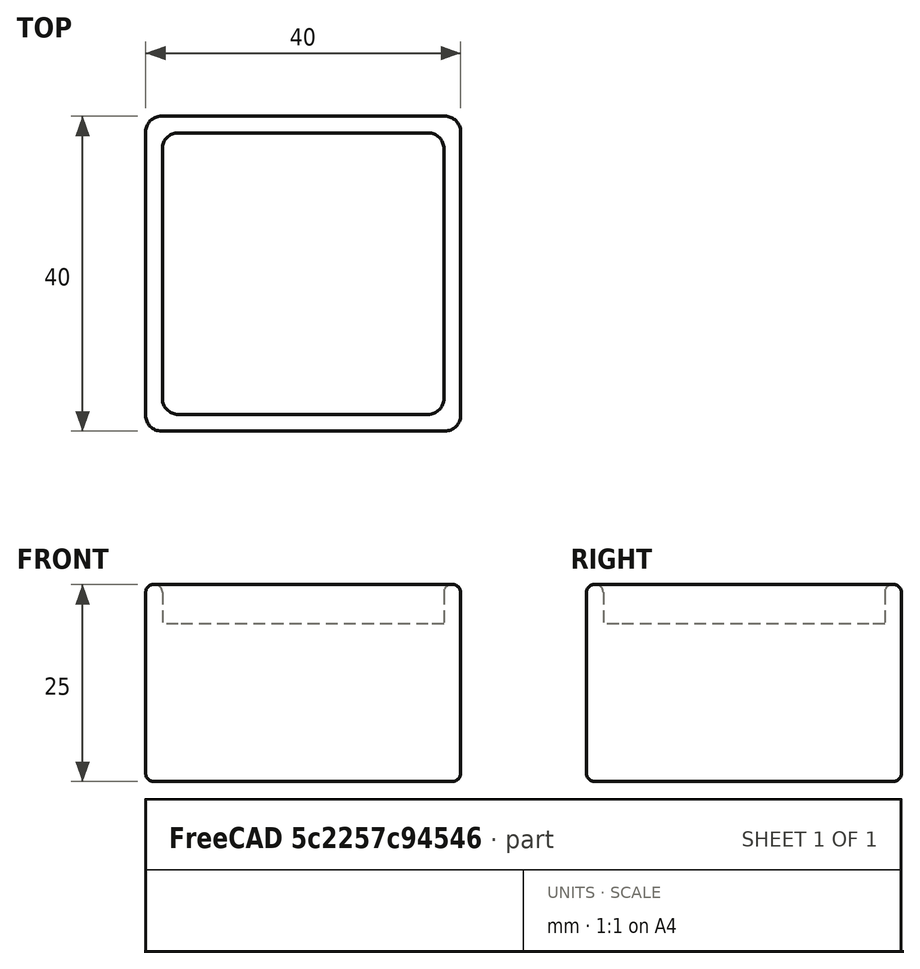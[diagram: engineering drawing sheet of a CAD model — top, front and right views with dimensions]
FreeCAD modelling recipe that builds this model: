
FCSTD DOCUMENT  (FreeCAD 0.21R33771 (Git))
Label: FurnitureGapPillars
License: All rights reserved
LicenseURL: http://en.wikipedia.org/wiki/All_rights_reserved
objects: Sketcher::SketchObject×2, PartDesign::Fillet×2, PartDesign::Pad×1, PartDesign::Pocket×1, PartDesign::Body×1, Mesh::Feature×1
note: 11 computed .brp shape members not serialized (recipe doc carries the construction recipe); baked Part::Feature solids carry a one-line shape summary decoded from their .brp

FEATURE [Sketcher::SketchObject] Sketch  label="BaseSketch"
  FullyConstrained = true
  MapMode = 5
  Support = -> [XY_Plane]
  sketch-geometry (5):
    g0: LineSegment StartX=-20 StartY=20 StartZ=0 EndX=-20 EndY=-20 EndZ=0
    g1: LineSegment StartX=-20 StartY=-20 StartZ=0 EndX=20 EndY=-20 EndZ=0
    g2: LineSegment StartX=20 StartY=-20 StartZ=0 EndX=20 EndY=20 EndZ=0
    g3: LineSegment StartX=20 StartY=20 StartZ=0 EndX=-20 EndY=20 EndZ=0
    g4: GeomPoint X=0 Y=0 Z=0
  constraints (12):
    c: Coincident(g0,g1)
    c: Coincident(g1,g2)
    c: Coincident(g2,g3)
    c: Coincident(g3,g0)
    c: Horizontal(g1)
    c: Horizontal(g3)
    c: Vertical(g0)
    c: Vertical(g2)
    c: Symmetric(g1,g0,g4)
    c: Coincident(g4,g-1)
    c: DistanceX(g1,g1) = 40
    c: DistanceY(g0,g0) = 40
FEATURE [PartDesign::Pad] Pad  label="BasePad"
  Direction = (0,0,1)
  Length = 25
  Length2 = 10
  Profile = -> Sketch
  ReferenceAxis = -> Sketch [N_Axis]
  Type = 0
FEATURE [Sketcher::SketchObject] Sketch001  label="BaseDentSketch"
  ExternalGeometry = -> [Pad]
  FullyConstrained = true
  MapMode = 5
  Placement = pos=(0,0,25) rot=(0,0,1;0rad)
  Support = -> [Pad]
  sketch-geometry (5):
    g0: LineSegment StartX=17.8787 StartY=-17.8787 StartZ=0 EndX=17.8787 EndY=17.8787 EndZ=0
    g1: LineSegment StartX=17.8787 StartY=17.8787 StartZ=0 EndX=-17.8787 EndY=17.8787 EndZ=0
    g2: LineSegment StartX=-17.8787 StartY=17.8787 StartZ=0 EndX=-17.8787 EndY=-17.8787 EndZ=0
    g3: LineSegment StartX=-17.8787 StartY=-17.8787 StartZ=0 EndX=17.8787 EndY=-17.8787 EndZ=0
    g4: GeomPoint X=-2e-16 Y=-2e-16 Z=0
  constraints (12):
    c: Coincident(g0,g1)
    c: Coincident(g1,g2)
    c: Coincident(g2,g3)
    c: Coincident(g3,g0)
    c: Horizontal(g1)
    c: Horizontal(g3)
    c: Vertical(g0)
    c: Vertical(g2)
    c: Symmetric(g1,g0,g4)
    c: Coincident(g4,g-1)
    c: Distance(g-3,g1) = 3
    c: Equal(g1,g0)
FEATURE [PartDesign::Pocket] Pocket  label="BaseDentPocket"
  BaseFeature = -> Pad
  Direction = (0,0,-1)
  Length = 5
  Length2 = 5
  Profile = -> Sketch001
  ReferenceAxis = -> Sketch001 [N_Axis]
  Type = 0
FEATURE [PartDesign::Fillet] Fillet  label="SideFillet"
  Base = -> Pocket [Edge8,Edge5,Edge1,Edge2,Edge17,Edge18,Edge22,Edge20]
  BaseFeature = -> Pocket
  Radius = 2
  SupportTransform = false
  UseAllEdges = false
FEATURE [PartDesign::Fillet] Fillet001  label="TopBottomFillet"
  Base = -> Fillet [Edge4,Edge1,Edge28]
  BaseFeature = -> Fillet
  Radius = 1
  SupportTransform = false
  UseAllEdges = false
FEATURE [PartDesign::Body] Body  label="FurnitureFoot"
  Group = -> [Sketch,Pad,Sketch001,Pocket,Fillet,Fillet001]
  Origin = -> Origin
  Tip = -> Fillet001
FEATURE [Mesh::Feature] Mesh  label="FurnitureFoot (Meshed)"
